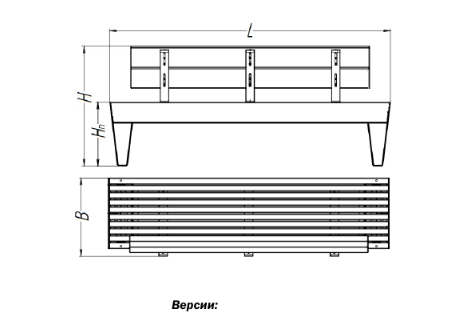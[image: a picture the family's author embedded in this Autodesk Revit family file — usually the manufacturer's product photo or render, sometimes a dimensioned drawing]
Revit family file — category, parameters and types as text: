
# Revit family: 22448 Скамейка стальная «Симпозиум» Хоббика
name_source: partatom
category: Антураж
revit_build: Autodesk Revit 2018 (Build: 20180423_1000(x64)
units: mm (PartAtom-declared; Revit-internal decimal feet)

## family parameters
Всегда вертикально = Да
Источник визуального образа = Геометрия семейства
На основе рабочей плоскости = Нет
Общий = Нет
При загрузке вырезать с полостями = Нет
Точка расчета площади = Нет

## types (6) — shared parameters
URL = https://hobbyka.ru
Артикул товара = Арт. 22448
Высота = 850 мм
Группа модели = Скамейки
Изготовитель = ООО «Хоббика»
Материал изделия = Сталь, дерево
Цвет лавки = Дерево
Цвет основания = Сталь
Ширина = 550 мм

## per-type parameters (varying)
| type | Версия 2,0 м (без подлокотников) | Версия 2,0 м (с подлокотниками и разделителем) | Версия 2,0 м (с подлокотниками) | Версия 4,0 м (двухсторонняя, без подлокотников) | Версия 4,0 м (двухсторонняя, с подлокотниками и разделителями) | Версия 4,0 м (двухсторонняя, с подлокотниками) | Длина | Изображение типоразмера | Описание |
| Версия 2,0 м (без подлокотников) | Да | Нет | Нет | Нет | Нет | Нет | 2000 мм | Скамейка стальная «Симпозиум» 2,0 м Арт 22448 БП.jpg | Скамейка стальная «Симпозиум». Версия 2,0 м без подлокотников |
| Версия 2,0 м (с подлокотниками) | Нет | Нет | Да | Нет | Нет | Нет | 2000 мм | Скамейка стальная «Симпозиум» 2,0 м Арт 22448 2П.jpg | Скамейка стальная «Симпозиум». Версия 2,0 м с подлокотниками |
| Версия 2,0 м (с подлокотниками и разделителем) | Нет | Да | Нет | Нет | Нет | Нет | 2000 мм | Скамейка стальная «Симпозиум» 2,0 м Арт 22448 2П+Р.jpg | Скамейка стальная «Симпозиум». Версия 2,0 м с подлокотниками и разделителем |
| Версия 4,0 м (двухсторонняя, без подлокотников) | Нет | Нет | Нет | Да | Нет | Нет | 4000 мм | Скамейка стальная «Симпозиум» 4,0 м Арт 22448 БП.jpg | Скамейка стальная «Симпозиум». Версия 4,0 м двухсторонняя, без подлокотников |
| Версия 4,0 м (двухсторонняя, с подлокотниками) | Нет | Нет | Нет | Нет | Нет | Да | 4000 мм | Скамейка стальная «Симпозиум» 4,0 м Арт 22448 2П+Р.jpg | Скамейка стальная «Симпозиум». Версия 4,0 м двухсторонняя, с подлокотниками |
| Версия 4,0 м (двухсторонняя, с подлокотниками и разделителями) | Нет | Нет | Нет | Нет | Да | Нет | 4000 мм | Скамейка стальная «Симпозиум» 4,0 м Арт 22448 2П+Р.jpg | Скамейка стальная «Симпозиум». Версия 4,0 м двухсторонняя, с подлокотниками и разделителями |
